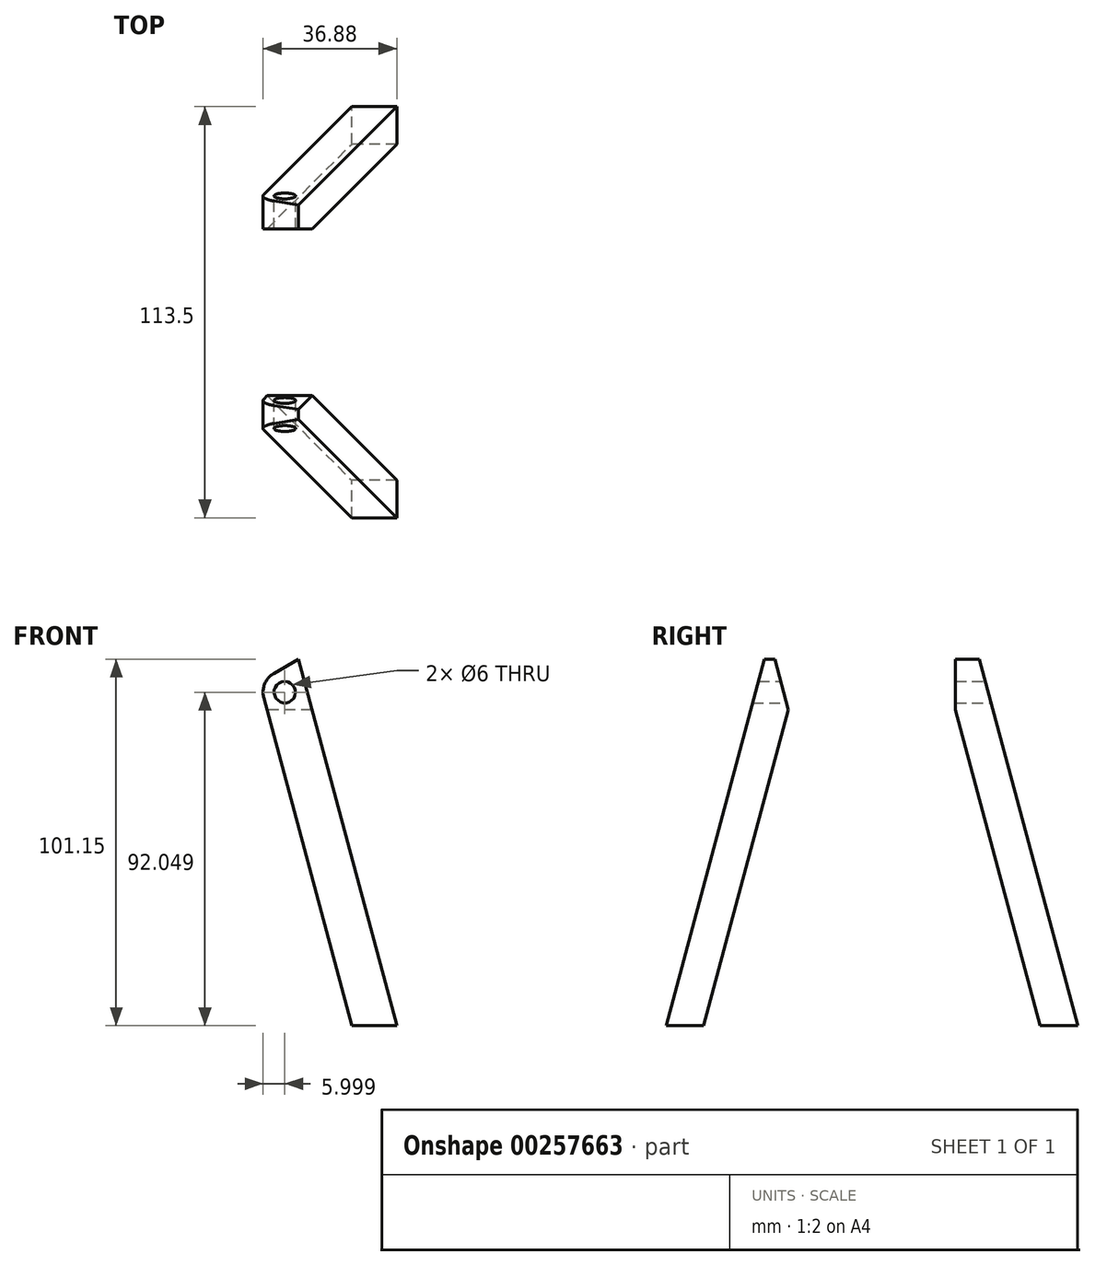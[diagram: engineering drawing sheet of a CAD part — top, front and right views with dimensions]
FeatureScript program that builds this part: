
annotation { "Feature Type Name" : "Feature", "Feature Type Description" : "" }
export const myFeature = defineFeature(function(context is Context, id is Id, definition is map)
    precondition{}
    {
        {
            var Q0;
            Q0=qCreatedBy(makeId("Front.planeOp"),FACE);
            var sketch = newSketch(context, id + "F0", { "sketchPlane" : qUnion([Q0])});
            skLineSegment(sketch, "E0.bottom", {"start": v(21.84, 19.65) * mm, "end": v(-24.84, 19.65) * mm});
            skLineSegment(sketch, "E0.top", {"start": v(24.84, -19.65) * mm, "end": v(-22.84, -19.65) * mm});
            skLineSegment(sketch, "E0.right", {"start": v(-24.84, 19.65) * mm, "end": v(-24.84, -16.19) * mm});
            skPoint(sketch, "E0.middle", {"position": v(0, 0) * mm});
            skLineSegment(sketch, "E1", {"start": v(21.84, 19.65) * mm, "end": v(24.84, 14.45) * mm});
            skLineSegment(sketch, "E2", {"start": v(24.84, 14.45) * mm, "end": v(7.51, 4.45) * mm});
            skLineSegment(sketch, "E3", {"start": v(7.51, 4.45) * mm, "end": v(14.76, -8.1) * mm});
            skLineSegment(sketch, "E4", {"start": v(14.76, -8.1) * mm, "end": v(24.64, -2.4) * mm});
            skLineSegment(sketch, "E5", {"start": v(24.64, -2.4) * mm, "end": v(24.84, -2.75) * mm});
            skLineSegment(sketch, "E6.trimOffspring", {"start": v(24.84, -2.75) * mm, "end": v(24.84, -19.65) * mm});
            skLineSegment(sketch, "E7", {"start": v(-24.84, -16.19) * mm, "end": v(-22.84, -19.65) * mm});
            skSolve(sketch);
        }
        {
            var Q0;
            Q0=makeQuery(id+"F0.imprint","IMPRINT",FACE,{"disambiguationData":[TD([[makeQuery(id+"F0.imprint","IMPRINT",EDGE,{"derivedFrom":sQuery(id+"F0.wireOp",EDGE,"E0.bottom")}),1.0]])]});
            extrude(context, id + "F1", {"entities" : qUnion([Q0]), "endBound" : BoundingType.SYMMETRIC, "depth" : 59.3 * mm});
        }
        {
            var Q0;
            Q0=makeQuery(id+"F1.opExtrude","SWEPT_FACE",FACE,{"disambiguationData":[OSD([sQuery(id+"F0.wireOp",EDGE,"E7")])]});
            var sketch = newSketch(context, id + "F2", { "sketchPlane" : qUnion([Q0])});
            skPoint(sketch, "E8", {"position": v(-22.65, -7.15) * mm});
            skPoint(sketch, "E9", {"position": v(22.65, -7.15) * mm});
            skSolve(sketch);
        }
        {
            var Q0;
            Q0=sQuery(id+"F2.wireOp",VERTEX,"E8");
            var Q1;
            Q1=sQuery(id+"F2.wireOp",VERTEX,"E9");
            var Q2;
            Q2=makeQuery(id+"F1.opExtrude","SWEPT_BODY",BODY,{"disambiguationData":[OSD([sQuery(id+"F0.wireOp",EDGE,"E0.bottom"),sQuery(id+"F0.wireOp",EDGE,"E0.top"),sQuery(id+"F0.wireOp",EDGE,"E0.right"),sQuery(id+"F0.wireOp",EDGE,"E1"),sQuery(id+"F0.wireOp",EDGE,"E2"),sQuery(id+"F0.wireOp",EDGE,"E3"),sQuery(id+"F0.wireOp",EDGE,"E4"),sQuery(id+"F0.wireOp",EDGE,"E5"),sQuery(id+"F0.wireOp",EDGE,"E6.trimOffspring"),sQuery(id+"F0.wireOp",EDGE,"E7")])]});
            hole(context, id + "F3", {"style" : HoleStyle.C_BORE, "endStyle" : HoleEndStyle.THROUGH, "holeDiameter" : 6.5 * mm, "cBoreDiameter" : 10 * mm, "cBoreDepth" : 20 * mm, "tappedDepth" : 15 * mm, "tapClearance" : 3, "startFromSketch" : true, "locations" : qUnion([Q0, Q1]), "scope" : qUnion([Q2])});
        }
        {
            var Q0;
            Q0=makeQuery(id+"F1.opExtrude","SWEPT_FACE",FACE,{"disambiguationData":[OSD([sQuery(id+"F0.wireOp",EDGE,"E0.bottom")])]});
            var sketch = newSketch(context, id + "F4", { "sketchPlane" : qUnion([Q0])});
            skCircle(sketch, "E10", {"center": v(-4.83, 9.65) * mm, "radius": 10 * mm});
            skCircle(sketch, "E11", {"center": v(-4.83, 9.65) * mm, "radius": 3 * mm});
            skLineSegment(sketch, "E12", {"start": v(-24.84, -29.65) * mm, "end": v(-24.84, 29.65) * mm});
            skLineSegment(sketch, "E13", {"start": v(21.84, -29.65) * mm, "end": v(-24.84, -29.65) * mm});
            skLineSegment(sketch, "E14", {"start": v(21.84, -29.65) * mm, "end": v(21.84, 29.65) * mm});
            skLineSegment(sketch, "E15", {"start": v(21.84, 29.65) * mm, "end": v(-24.84, 29.65) * mm});
            skCircle(sketch, "E16", {"center": v(-4.83, 9.65) * mm, "radius": 16 * mm});
            skCircle(sketch, "E17", {"center": v(-4.83, 9.65) * mm, "radius": 12.5 * mm});
            skSolve(sketch);
        }
        {
            var Q0;
            Q0=makeQuery(id+"F4.imprint","IMPRINT",FACE,{"disambiguationData":[TD([[makeQuery(id+"F4.imprint","IMPRINT",EDGE,{"derivedFrom":sQuery(id+"F4.wireOp",EDGE,"E10")}),1.0]])]});
            var Q1;
            Q1=makeQuery(id+"F4.imprint","IMPRINT",FACE,{"disambiguationData":[TD([[makeQuery(id+"F4.imprint","IMPRINT",EDGE,{"derivedFrom":sQuery(id+"F4.wireOp",EDGE,"E10")}),-1.0]])]});
            var Q2;
            Q2=makeQuery(id+"F4.imprint","IMPRINT",FACE,{"disambiguationData":[TD([[makeQuery(id+"F4.imprint","IMPRINT",EDGE,{"derivedFrom":sQuery(id+"F4.wireOp",EDGE,"E16")}),1.0]])]});
            var Q3;
            Q3=makeQuery(id+"F4.imprint","IMPRINT",FACE,{"disambiguationData":[TD([[makeQuery(id+"F4.imprint","IMPRINT",EDGE,{"derivedFrom":sQuery(id+"F4.wireOp",EDGE,"E11")}),1.0]])]});
            extrude(context, id + "F5", {"entities" : qUnion([Q0, Q1, Q2, Q3]), "operationType" : NewBodyOperationType.REMOVE, "oppositeDirection" : true, "depth" : 15 * mm});
        }
        {
            var Q0;
            Q0=makeQuery(id+"F4.imprint","IMPRINT",FACE,{"disambiguationData":[TD([[makeQuery(id+"F4.imprint","IMPRINT",EDGE,{"derivedFrom":sQuery(id+"F4.wireOp",EDGE,"E16")}),1.0]])]});
            var Q1;
            Q1=makeQuery(id+"F4.imprint","IMPRINT",FACE,{"disambiguationData":[TD([[makeQuery(id+"F4.imprint","IMPRINT",EDGE,{"derivedFrom":sQuery(id+"F4.wireOp",EDGE,"E10")}),-1.0]])]});
            extrude(context, id + "F6", {"entities" : qUnion([Q0, Q1]), "oppositeDirection" : true, "depth" : 15 * mm});
        }
        {
            var Q0;
            Q0=makeQuery(id+"F4.imprint","IMPRINT",FACE,{"disambiguationData":[TD([[makeQuery(id+"F4.imprint","IMPRINT",EDGE,{"derivedFrom":sQuery(id+"F4.wireOp",EDGE,"E10")}),-1.0]])]});
            extrude(context, id + "F7", {"entities" : qUnion([Q0]), "operationType" : NewBodyOperationType.ADD, "depth" : 25 * mm});
        }
        {
            var Q0;
            Q0=makeQuery(id+"F7.opExtrude","CAP_EDGE",EDGE,{"disambiguationData":[OSD([sQuery(id+"F4.wireOp",EDGE,"E17")])],"isStart":false});
            var Q1;
            Q1=makeQuery(id+"F7.opExtrude","CAP_EDGE",EDGE,{"disambiguationData":[OSD([sQuery(id+"F4.wireOp",EDGE,"E10")])],"isStart":false});
            var Q2;
            Q2=makeQuery(id+"F7.opExtrude","CAP_EDGE",EDGE,{"disambiguationData":[OSD([sQuery(id+"F4.wireOp",EDGE,"E17")])],"isStart":true});
            var Q3;
            Q3=makeQuery(id+"F5.boolean.opBoolean","COPY",EDGE,{"derivedFrom":makeQuery(id+"F5.opExtrude","CAP_EDGE",EDGE,{"disambiguationData":[OSD([sQuery(id+"F4.wireOp",EDGE,"E16")])],"isStart":true})});
            chamfer(context, id + "F8", {"entities" : qUnion([Q0, Q1, Q2, Q3]), "width" : 0.2 * mm, "tangentPropagation" : true});
        }
        {
            var Q0;
            Q0=makeQuery(id+"F4.imprint","IMPRINT",FACE,{"disambiguationData":[TD([[makeQuery(id+"F4.imprint","IMPRINT",EDGE,{"derivedFrom":sQuery(id+"F4.wireOp",EDGE,"E10")}),1.0]])]});
            var Q1;
            Q1=makeQuery(id+"F4.imprint","IMPRINT",FACE,{"disambiguationData":[TD([[makeQuery(id+"F4.imprint","IMPRINT",EDGE,{"derivedFrom":sQuery(id+"F4.wireOp",EDGE,"E11")}),1.0]])]});
            extrude(context, id + "F9", {"entities" : qUnion([Q0, Q1]), "depth" : 205 * mm, "hasSecondDirection" : true, "secondDirectionOppositeDirection" : true, "secondDirectionDepth" : 15 * mm});
        }
        {
            var Q0;
            Q0=makeQuery(id+"F9.opExtrude","CAP_EDGE",EDGE,{"disambiguationData":[OSD([sQuery(id+"F4.wireOp",EDGE,"E10")])],"isStart":false});
            var Q1;
            Q1=makeQuery(id+"F9.opExtrude","CAP_EDGE",EDGE,{"disambiguationData":[OSD([sQuery(id+"F4.wireOp",EDGE,"E10")])],"isStart":true});
            chamfer(context, id + "F10", {"entities" : qUnion([Q0, Q1]), "width" : 0.75 * mm, "tangentPropagation" : true});
        }
        {
            var Q0;
            Q0=qCreatedBy(makeId("Front.planeOp"),FACE);
            var sketch = newSketch(context, id + "F11", { "sketchPlane" : qUnion([Q0])});
            skPoint(sketch, "E18.0", {"position": v(14.76, -8.1) * mm});
            skPoint(sketch, "E19.0", {"position": v(24.64, -2.4) * mm});
            skPoint(sketch, "E20.0", {"position": v(24.84, 14.45) * mm});
            skPoint(sketch, "E21.0", {"position": v(7.51, 4.45) * mm});
            skLineSegment(sketch, "E22", {"start": v(14.76, -8.1) * mm, "end": v(196.63, 96.9) * mm, "construction": true});
            skLineSegment(sketch, "E23", {"start": v(7.51, 4.45) * mm, "end": v(189.38, 109.45) * mm, "construction": true});
            skLineSegment(sketch, "E24", {"start": v(189.38, 109.45) * mm, "end": v(196.63, 96.9) * mm, "construction": true});
            skLineSegment(sketch, "E25", {"start": v(29.76, -19.65) * mm, "end": v(244.06, -19.65) * mm, "construction": true});
            skLineSegment(sketch, "E26.0", {"start": v(24.84, -19.65) * mm, "end": v(-22.84, -19.65) * mm, "construction": true});
            skLineSegment(sketch, "E27", {"start": v(169.97, 81.5) * mm, "end": v(197.08, -19.65) * mm});
            skLineSegment(sketch, "E28", {"start": v(160.4, 70.85) * mm, "end": v(184.65, -19.65) * mm});
            skLineSegment(sketch, "E29", {"start": v(159.21, 75.3) * mm, "end": v(169.97, 81.5) * mm});
            skLineSegment(sketch, "E30", {"start": v(164.65, 78.2) * mm, "end": v(170.44, 79.75) * mm, "construction": true});
            skPoint(sketch, "E31.visualSharp", {"position": v(159.21, 75.3) * mm});
            skArc(sketch, "E31.filletArc", {"start": v(164.65, 78.2) * mm, "mid": v(161, 75.4) * mm, "end": v(160.4, 70.85) * mm});
            skCircle(sketch, "E32", {"center": v(166.2, 72.4) * mm, "radius": 3 * mm});
            skLineSegment(sketch, "E33", {"start": v(184.65, -19.65) * mm, "end": v(197.08, -19.65) * mm});
            skPoint(sketch, "E34", {"position": v(163.2, 77.6) * mm});
            skSolve(sketch);
        }
        {
            var Q0;
            {var subQ4=sQuery(id+"F11.wireOp",EDGE,"E27");Q0=makeQuery(id+"F11.imprint","IMPRINT",FACE,{"disambiguationData":[TD([[makeQuery(id+"F11.imprint","IMPRINT",EDGE,{"derivedFrom":subQ4}),-1.0]])]});}
            extrude(context, id + "F12", {"entities" : qUnion([Q0]), "endBound" : BoundingType.SYMMETRIC, "depth" : 120 * mm});
        }
        {
            var Q0;
            Q0=qCreatedBy(makeId("Right.planeOp"),FACE);
            var sketch = newSketch(context, id + "F13", { "sketchPlane" : qUnion([Q0])});
            skPoint(sketch, "E35.0", {"position": v(-60, -19.65) * mm});
            skPoint(sketch, "E36.0", {"position": v(60, -19.65) * mm});
            skLineSegment(sketch, "E37.0", {"start": v(-29.65, 19.65) * mm, "end": v(-29.65, -16.19) * mm, "construction": true});
            skLineSegment(sketch, "E38.0", {"start": v(29.65, 19.65) * mm, "end": v(29.65, -16.19) * mm, "construction": true});
            skLineSegment(sketch, "E39", {"start": v(-29.65, 19.65) * mm, "end": v(-29.65, 81.5) * mm, "construction": true});
            skLineSegment(sketch, "E40", {"start": v(29.65, 19.65) * mm, "end": v(29.65, 81.5) * mm, "construction": true});
            skLineSegment(sketch, "E41", {"start": v(-46.4, -19.65) * mm, "end": v(-23.05, 67.5) * mm});
            skLineSegment(sketch, "E42", {"start": v(-56.75, -19.65) * mm, "end": v(-29.65, 81.5) * mm});
            skLineSegment(sketch, "E43", {"start": v(-33.4, 67.5) * mm, "end": v(-23.05, 67.5) * mm, "construction": true});
            skLineSegment(sketch, "E44", {"start": v(-23.05, 67.5) * mm, "end": v(-23.05, 81.5) * mm, "construction": true});
            skLineSegment(sketch, "E45", {"start": v(-23.05, 81.5) * mm, "end": v(-29.65, 81.5) * mm});
            skPoint(sketch, "E46.orphan", {"position": v(-19.3, 81.5) * mm});
            skLineSegment(sketch, "E47", {"start": v(-56.75, -19.65) * mm, "end": v(-46.4, -19.65) * mm});
            skLineSegment(sketch, "E48.MirrorCS", {"start": v(46.4, -19.65) * mm, "end": v(23.05, 67.5) * mm});
            skPoint(sketch, "E49.MirrorP", {"position": v(19.3, 81.5) * mm});
            skLineSegment(sketch, "E50.MirrorCS", {"start": v(56.75, -19.65) * mm, "end": v(29.65, 81.5) * mm});
            skLineSegment(sketch, "E51.MirrorCS", {"start": v(56.75, -19.65) * mm, "end": v(46.4, -19.65) * mm});
            skLineSegment(sketch, "E52.MirrorCS", {"start": v(23.05, 67.5) * mm, "end": v(23.05, 81.5) * mm});
            skLineSegment(sketch, "E53.MirrorCS", {"start": v(33.4, 67.5) * mm, "end": v(23.05, 67.5) * mm, "construction": true});
            skLineSegment(sketch, "E54.MirrorCS", {"start": v(23.05, 81.5) * mm, "end": v(29.65, 81.5) * mm});
            skLineSegment(sketch, "E55", {"start": v(-26.8, 81.5) * mm, "end": v(-23.05, 67.5) * mm});
            skSolve(sketch);
        }
        {
            var Q0;
            Q0=makeQuery(id+"F13.imprint","IMPRINT",FACE,{"disambiguationData":[TD([[makeQuery(id+"F13.imprint","IMPRINT",EDGE,{"derivedFrom":sQuery(id+"F13.wireOp",EDGE,"E41")}),1.0]])]});
            var Q1;
            Q1=makeQuery(id+"F13.imprint","IMPRINT",FACE,{"disambiguationData":[TD([[makeQuery(id+"F13.imprint","IMPRINT",EDGE,{"derivedFrom":sQuery(id+"F13.wireOp",EDGE,"E48.MirrorCS")}),-1.0]])]});
            extrude(context, id + "F14", {"entities" : qUnion([Q0, Q1]), "operationType" : NewBodyOperationType.INTERSECT, "endBound" : BoundingType.THROUGH_ALL, "depth" : 25 * mm});
        }
    });
